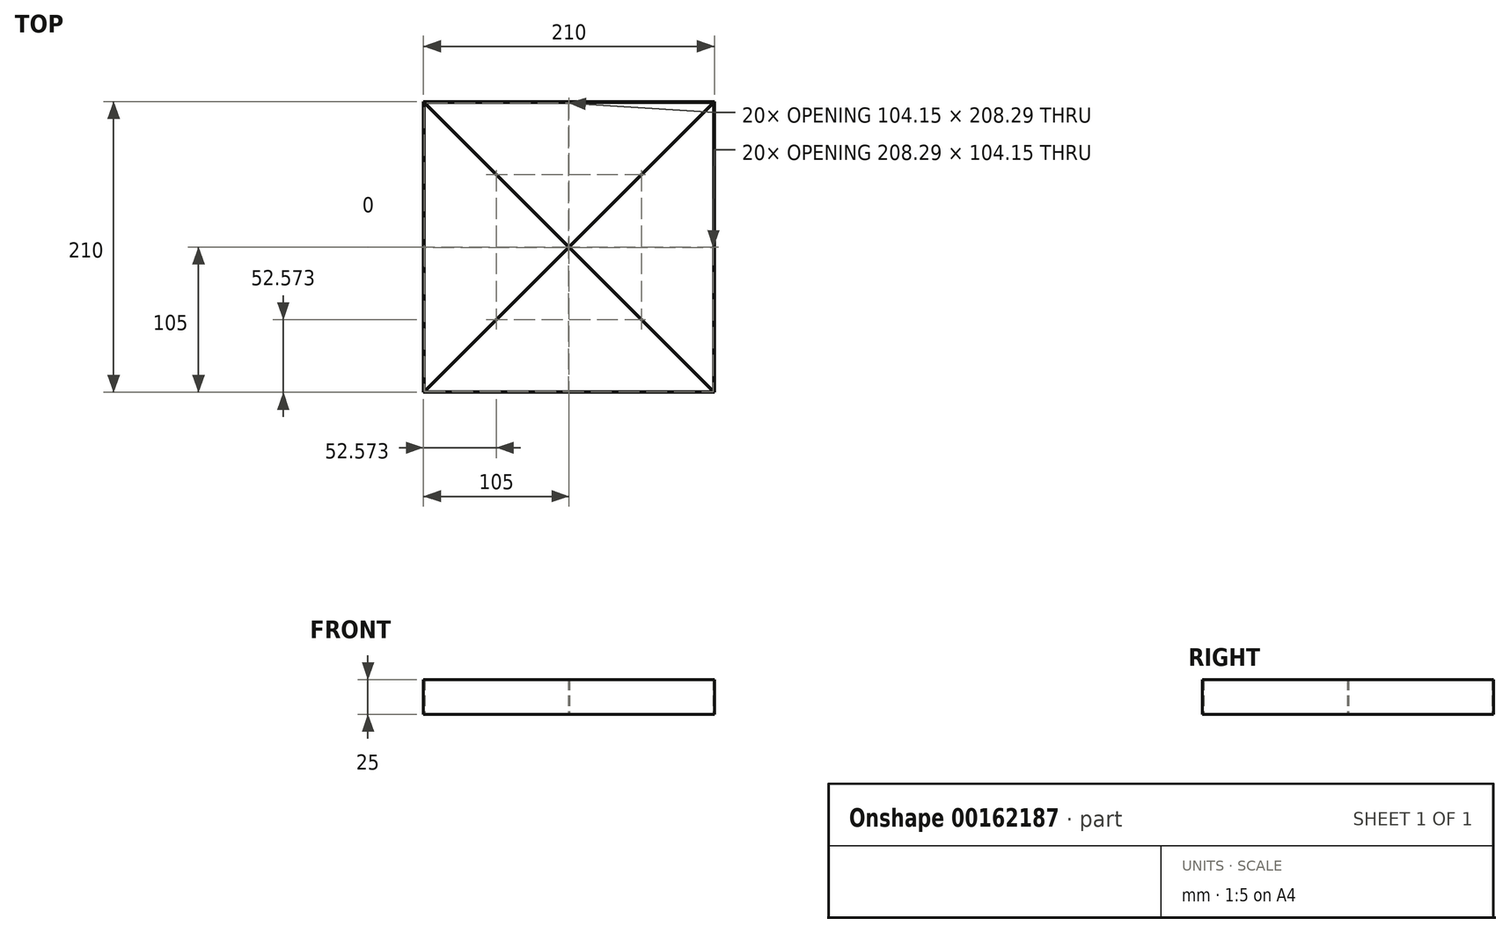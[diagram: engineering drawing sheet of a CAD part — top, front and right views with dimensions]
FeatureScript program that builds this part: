
annotation { "Feature Type Name" : "Feature", "Feature Type Description" : "" }
export const myFeature = defineFeature(function(context is Context, id is Id, definition is map)
    precondition{}
    {
        {
            var Q0;
            Q0=qCreatedBy(makeId("Top.planeOp"),FACE);
            var sketch = newSketch(context, id + "F0", { "sketchPlane" : qUnion([Q0])});
            skLineSegment(sketch, "E0.bottom", {"start": v(-105, 105) * mm, "end": v(105, 105) * mm});
            skLineSegment(sketch, "E0.top", {"start": v(-105, -105) * mm, "end": v(105, -105) * mm});
            skLineSegment(sketch, "E0.left", {"start": v(-105, 105) * mm, "end": v(-105, -105) * mm});
            skLineSegment(sketch, "E0.right", {"start": v(105, 105) * mm, "end": v(105, -105) * mm});
            skPoint(sketch, "E0.middle", {"position": v(0, 0) * mm});
            skLineSegment(sketch, "E1", {"start": v(-105, 105) * mm, "end": v(105, -105) * mm});
            skLineSegment(sketch, "E2", {"start": v(105, 105) * mm, "end": v(-105, -105) * mm});
            skLineSegment(sketch, "E3.bottom", {"start": v(-104.5, 104.5) * mm, "end": v(104.5, 104.5) * mm});
            skLineSegment(sketch, "E3.top", {"start": v(-104.5, -104.5) * mm, "end": v(104.5, -104.5) * mm});
            skLineSegment(sketch, "E3.left", {"start": v(-104.5, 104.5) * mm, "end": v(-104.5, -104.5) * mm});
            skLineSegment(sketch, "E3.right", {"start": v(104.5, 104.5) * mm, "end": v(104.5, -104.5) * mm});
            skLineSegment(sketch, "E4", {"start": v(-104.65, 105) * mm, "end": v(105, -104.65) * mm});
            skLineSegment(sketch, "E5", {"start": v(-105, 104.65) * mm, "end": v(104.65, -105) * mm});
            skLineSegment(sketch, "E6", {"start": v(-105, -104.65) * mm, "end": v(104.65, 105) * mm});
            skLineSegment(sketch, "E7", {"start": v(105, 104.65) * mm, "end": v(-104.65, -105) * mm});
            skSolve(sketch);
        }
        {
            var Q0;
            {var subQ0=sQuery(id+"F0.wireOp",EDGE,"E5");var subQ1=sQuery(id+"F0.wireOp",EDGE,"E0.left");var subQ2=makeQuery(id+"F0.imprint","INTERSECT",VERTEX,{"derivedFrom":[subQ1,subQ0]});Q0=makeQuery(id+"F0.imprint","IMPRINT",FACE,{"disambiguationData":[TD([[makeQuery(id+"F0.imprint","IMPRINT",EDGE,{"disambiguationData":[TD([[subQ2,-1.0]])],"derivedFrom":subQ1}),1.0]])]});}
            var Q1;
            {var subQ0=sQuery(id+"F0.wireOp",EDGE,"E5");var subQ1=sQuery(id+"F0.wireOp",EDGE,"E0.top");var subQ2=makeQuery(id+"F0.imprint","INTERSECT",VERTEX,{"derivedFrom":[subQ1,subQ0]});Q1=makeQuery(id+"F0.imprint","IMPRINT",FACE,{"disambiguationData":[TD([[makeQuery(id+"F0.imprint","IMPRINT",EDGE,{"disambiguationData":[TD([[subQ2,1.0]])],"derivedFrom":subQ1}),1.0]])]});}
            var Q2;
            {var subQ1=sQuery(id+"F0.wireOp",EDGE,"E0.top");var subQ3=sQuery(id+"F0.wireOp",EDGE,"E7");var subQ4=makeQuery(id+"F0.imprint","INTERSECT",VERTEX,{"derivedFrom":[subQ1,subQ3]});Q2=makeQuery(id+"F0.imprint","IMPRINT",FACE,{"disambiguationData":[TD([[makeQuery(id+"F0.imprint","IMPRINT",EDGE,{"disambiguationData":[TD([[subQ4,1.0]])],"derivedFrom":subQ3}),-1.0]])]});}
            var Q3;
            {var subQ1=sQuery(id+"F0.wireOp",EDGE,"E0.left");var subQ3=sQuery(id+"F0.wireOp",EDGE,"E6");var subQ4=makeQuery(id+"F0.imprint","INTERSECT",VERTEX,{"derivedFrom":[subQ1,subQ3]});Q3=makeQuery(id+"F0.imprint","IMPRINT",FACE,{"disambiguationData":[TD([[makeQuery(id+"F0.imprint","IMPRINT",EDGE,{"disambiguationData":[TD([[subQ4,-1.0]])],"derivedFrom":subQ3}),-1.0]])]});}
            var Q4;
            {var subQ1=sQuery(id+"F0.wireOp",EDGE,"E2");var subQ3=sQuery(id+"F0.wireOp",EDGE,"E5");var subQ4=makeQuery(id+"F0.imprint","INTERSECT",VERTEX,{"derivedFrom":[subQ1,subQ3]});Q4=makeQuery(id+"F0.imprint","IMPRINT",FACE,{"disambiguationData":[TD([[makeQuery(id+"F0.imprint","IMPRINT",EDGE,{"disambiguationData":[TD([[subQ4,-1.0]])],"derivedFrom":subQ3}),-1.0]])]});}
            var Q5;
            {var subQ1=sQuery(id+"F0.wireOp",EDGE,"E2");var subQ3=sQuery(id+"F0.wireOp",EDGE,"E5");var subQ4=makeQuery(id+"F0.imprint","INTERSECT",VERTEX,{"derivedFrom":[subQ1,subQ3]});Q5=makeQuery(id+"F0.imprint","IMPRINT",FACE,{"disambiguationData":[TD([[makeQuery(id+"F0.imprint","IMPRINT",EDGE,{"disambiguationData":[TD([[subQ4,1.0]])],"derivedFrom":subQ3}),-1.0]])]});}
            var Q6;
            {var subQ0=sQuery(id+"F0.wireOp",EDGE,"E4");var subQ1=sQuery(id+"F0.wireOp",EDGE,"E0.right");var subQ2=makeQuery(id+"F0.imprint","INTERSECT",VERTEX,{"derivedFrom":[subQ1,subQ0]});Q6=makeQuery(id+"F0.imprint","IMPRINT",FACE,{"disambiguationData":[TD([[makeQuery(id+"F0.imprint","IMPRINT",EDGE,{"disambiguationData":[TD([[subQ2,1.0]])],"derivedFrom":subQ1}),-1.0]])]});}
            var Q7;
            {var subQ1=sQuery(id+"F0.wireOp",EDGE,"E0.right");var subQ3=sQuery(id+"F0.wireOp",EDGE,"E4");var subQ4=makeQuery(id+"F0.imprint","INTERSECT",VERTEX,{"derivedFrom":[subQ1,subQ3]});Q7=makeQuery(id+"F0.imprint","IMPRINT",FACE,{"disambiguationData":[TD([[makeQuery(id+"F0.imprint","IMPRINT",EDGE,{"disambiguationData":[TD([[subQ4,1.0]])],"derivedFrom":subQ3}),-1.0]])]});}
            var Q8;
            {var subQ1=sQuery(id+"F0.wireOp",EDGE,"E0.top");var subQ3=sQuery(id+"F0.wireOp",EDGE,"E5");var subQ4=makeQuery(id+"F0.imprint","INTERSECT",VERTEX,{"derivedFrom":[subQ1,subQ3]});Q8=makeQuery(id+"F0.imprint","IMPRINT",FACE,{"disambiguationData":[TD([[makeQuery(id+"F0.imprint","IMPRINT",EDGE,{"disambiguationData":[TD([[subQ4,1.0]])],"derivedFrom":subQ3}),1.0]])]});}
            var Q9;
            {var subQ0=sQuery(id+"F0.wireOp",EDGE,"E3.top");var subQ5=sQuery(id+"F0.wireOp",EDGE,"E5");var subQ6=makeQuery(id+"F0.imprint","INTERSECT",VERTEX,{"derivedFrom":[subQ0,subQ5]});Q9=makeQuery(id+"F0.imprint","IMPRINT",FACE,{"disambiguationData":[TD([[makeQuery(id+"F0.imprint","IMPRINT",EDGE,{"disambiguationData":[TD([[subQ6,1.0]])],"derivedFrom":subQ5}),1.0]])]});}
            var Q10;
            {var subQ0=sQuery(id+"F0.wireOp",EDGE,"E3.right");var subQ5=sQuery(id+"F0.wireOp",EDGE,"E4");var subQ7=makeQuery(id+"F0.imprint","INTERSECT",VERTEX,{"derivedFrom":[subQ0,subQ5]});Q10=makeQuery(id+"F0.imprint","IMPRINT",FACE,{"disambiguationData":[TD([[makeQuery(id+"F0.imprint","IMPRINT",EDGE,{"disambiguationData":[TD([[subQ7,1.0]])],"derivedFrom":subQ5}),-1.0]])]});}
            var Q11;
            {var subQ0=sQuery(id+"F0.wireOp",EDGE,"E6");var subQ1=sQuery(id+"F0.wireOp",EDGE,"E1");var subQ2=makeQuery(id+"F0.imprint","INTERSECT",VERTEX,{"derivedFrom":[subQ1,subQ0]});Q11=makeQuery(id+"F0.imprint","IMPRINT",FACE,{"disambiguationData":[TD([[makeQuery(id+"F0.imprint","IMPRINT",EDGE,{"disambiguationData":[TD([[subQ2,-1.0]])],"derivedFrom":subQ1}),-1.0]])]});}
            var Q12;
            {var subQ0=sQuery(id+"F0.wireOp",EDGE,"E2");var subQ1=sQuery(id+"F0.wireOp",EDGE,"E1");var subQ2=makeQuery(id+"F0.imprint","INTERSECT",VERTEX,{"derivedFrom":[subQ1,subQ0]});Q12=makeQuery(id+"F0.imprint","IMPRINT",FACE,{"disambiguationData":[TD([[makeQuery(id+"F0.imprint","IMPRINT",EDGE,{"disambiguationData":[TD([[subQ2,-1.0]])],"derivedFrom":subQ1}),-1.0]])]});}
            var Q13;
            {var subQ0=sQuery(id+"F0.wireOp",EDGE,"E2");var subQ1=sQuery(id+"F0.wireOp",EDGE,"E1");var subQ2=makeQuery(id+"F0.imprint","INTERSECT",VERTEX,{"derivedFrom":[subQ1,subQ0]});Q13=makeQuery(id+"F0.imprint","IMPRINT",FACE,{"disambiguationData":[TD([[makeQuery(id+"F0.imprint","IMPRINT",EDGE,{"disambiguationData":[TD([[subQ2,-1.0]])],"derivedFrom":subQ1}),1.0]])]});}
            var Q14;
            {var subQ0=sQuery(id+"F0.wireOp",EDGE,"E6");var subQ1=sQuery(id+"F0.wireOp",EDGE,"E1");var subQ2=makeQuery(id+"F0.imprint","INTERSECT",VERTEX,{"derivedFrom":[subQ1,subQ0]});Q14=makeQuery(id+"F0.imprint","IMPRINT",FACE,{"disambiguationData":[TD([[makeQuery(id+"F0.imprint","IMPRINT",EDGE,{"disambiguationData":[TD([[subQ2,-1.0]])],"derivedFrom":subQ1}),1.0]])]});}
            var Q15;
            {var subQ1=sQuery(id+"F0.wireOp",EDGE,"E2");var subQ3=sQuery(id+"F0.wireOp",EDGE,"E4");var subQ4=makeQuery(id+"F0.imprint","INTERSECT",VERTEX,{"derivedFrom":[subQ1,subQ3]});Q15=makeQuery(id+"F0.imprint","IMPRINT",FACE,{"disambiguationData":[TD([[makeQuery(id+"F0.imprint","IMPRINT",EDGE,{"disambiguationData":[TD([[subQ4,-1.0]])],"derivedFrom":subQ3}),1.0]])]});}
            var Q16;
            {var subQ1=sQuery(id+"F0.wireOp",EDGE,"E2");var subQ3=sQuery(id+"F0.wireOp",EDGE,"E4");var subQ4=makeQuery(id+"F0.imprint","INTERSECT",VERTEX,{"derivedFrom":[subQ1,subQ3]});Q16=makeQuery(id+"F0.imprint","IMPRINT",FACE,{"disambiguationData":[TD([[makeQuery(id+"F0.imprint","IMPRINT",EDGE,{"disambiguationData":[TD([[subQ4,1.0]])],"derivedFrom":subQ3}),1.0]])]});}
            var Q17;
            {var subQ0=sQuery(id+"F0.wireOp",EDGE,"E3.bottom");var subQ5=sQuery(id+"F0.wireOp",EDGE,"E4");var subQ6=makeQuery(id+"F0.imprint","INTERSECT",VERTEX,{"derivedFrom":[subQ0,subQ5]});Q17=makeQuery(id+"F0.imprint","IMPRINT",FACE,{"disambiguationData":[TD([[makeQuery(id+"F0.imprint","IMPRINT",EDGE,{"disambiguationData":[TD([[subQ6,-1.0]])],"derivedFrom":subQ5}),-1.0]])]});}
            var Q18;
            {var subQ0=sQuery(id+"F0.wireOp",EDGE,"E3.left");var subQ5=sQuery(id+"F0.wireOp",EDGE,"E5");var subQ6=makeQuery(id+"F0.imprint","INTERSECT",VERTEX,{"derivedFrom":[subQ0,subQ5]});Q18=makeQuery(id+"F0.imprint","IMPRINT",FACE,{"disambiguationData":[TD([[makeQuery(id+"F0.imprint","IMPRINT",EDGE,{"disambiguationData":[TD([[subQ6,-1.0]])],"derivedFrom":subQ5}),1.0]])]});}
            var Q19;
            {var subQ1=sQuery(id+"F0.wireOp",EDGE,"E0.left");var subQ3=sQuery(id+"F0.wireOp",EDGE,"E5");var subQ4=makeQuery(id+"F0.imprint","INTERSECT",VERTEX,{"derivedFrom":[subQ1,subQ3]});Q19=makeQuery(id+"F0.imprint","IMPRINT",FACE,{"disambiguationData":[TD([[makeQuery(id+"F0.imprint","IMPRINT",EDGE,{"disambiguationData":[TD([[subQ4,-1.0]])],"derivedFrom":subQ3}),1.0]])]});}
            var Q20;
            {var subQ1=sQuery(id+"F0.wireOp",EDGE,"E0.bottom");var subQ3=sQuery(id+"F0.wireOp",EDGE,"E4");var subQ4=makeQuery(id+"F0.imprint","INTERSECT",VERTEX,{"derivedFrom":[subQ1,subQ3]});Q20=makeQuery(id+"F0.imprint","IMPRINT",FACE,{"disambiguationData":[TD([[makeQuery(id+"F0.imprint","IMPRINT",EDGE,{"disambiguationData":[TD([[subQ4,-1.0]])],"derivedFrom":subQ3}),-1.0]])]});}
            var Q21;
            {var subQ0=sQuery(id+"F0.wireOp",EDGE,"E4");var subQ1=sQuery(id+"F0.wireOp",EDGE,"E0.bottom");var subQ2=makeQuery(id+"F0.imprint","INTERSECT",VERTEX,{"derivedFrom":[subQ1,subQ0]});Q21=makeQuery(id+"F0.imprint","IMPRINT",FACE,{"disambiguationData":[TD([[makeQuery(id+"F0.imprint","IMPRINT",EDGE,{"disambiguationData":[TD([[subQ2,-1.0]])],"derivedFrom":subQ1}),-1.0]])]});}
            var Q22;
            {var subQ1=sQuery(id+"F0.wireOp",EDGE,"E0.bottom");var subQ3=sQuery(id+"F0.wireOp",EDGE,"E6");var subQ4=makeQuery(id+"F0.imprint","INTERSECT",VERTEX,{"derivedFrom":[subQ1,subQ3]});Q22=makeQuery(id+"F0.imprint","IMPRINT",FACE,{"disambiguationData":[TD([[makeQuery(id+"F0.imprint","IMPRINT",EDGE,{"disambiguationData":[TD([[subQ4,1.0]])],"derivedFrom":subQ3}),-1.0]])]});}
            var Q23;
            {var subQ1=sQuery(id+"F0.wireOp",EDGE,"E0.right");var subQ3=sQuery(id+"F0.wireOp",EDGE,"E7");var subQ4=makeQuery(id+"F0.imprint","INTERSECT",VERTEX,{"derivedFrom":[subQ1,subQ3]});Q23=makeQuery(id+"F0.imprint","IMPRINT",FACE,{"disambiguationData":[TD([[makeQuery(id+"F0.imprint","IMPRINT",EDGE,{"disambiguationData":[TD([[subQ4,-1.0]])],"derivedFrom":subQ3}),-1.0]])]});}
            extrude(context, id + "F1", {"entities" : qUnion([Q0, Q1, Q2, Q3, Q4, Q5, Q6, Q7, Q8, Q9, Q10, Q11, Q12, Q13, Q14, Q15, Q16, Q17, Q18, Q19, Q20, Q21, Q22, Q23]), "depth" : 25 * mm, "offsetDistance" : 25 * mm});
        }
    });
